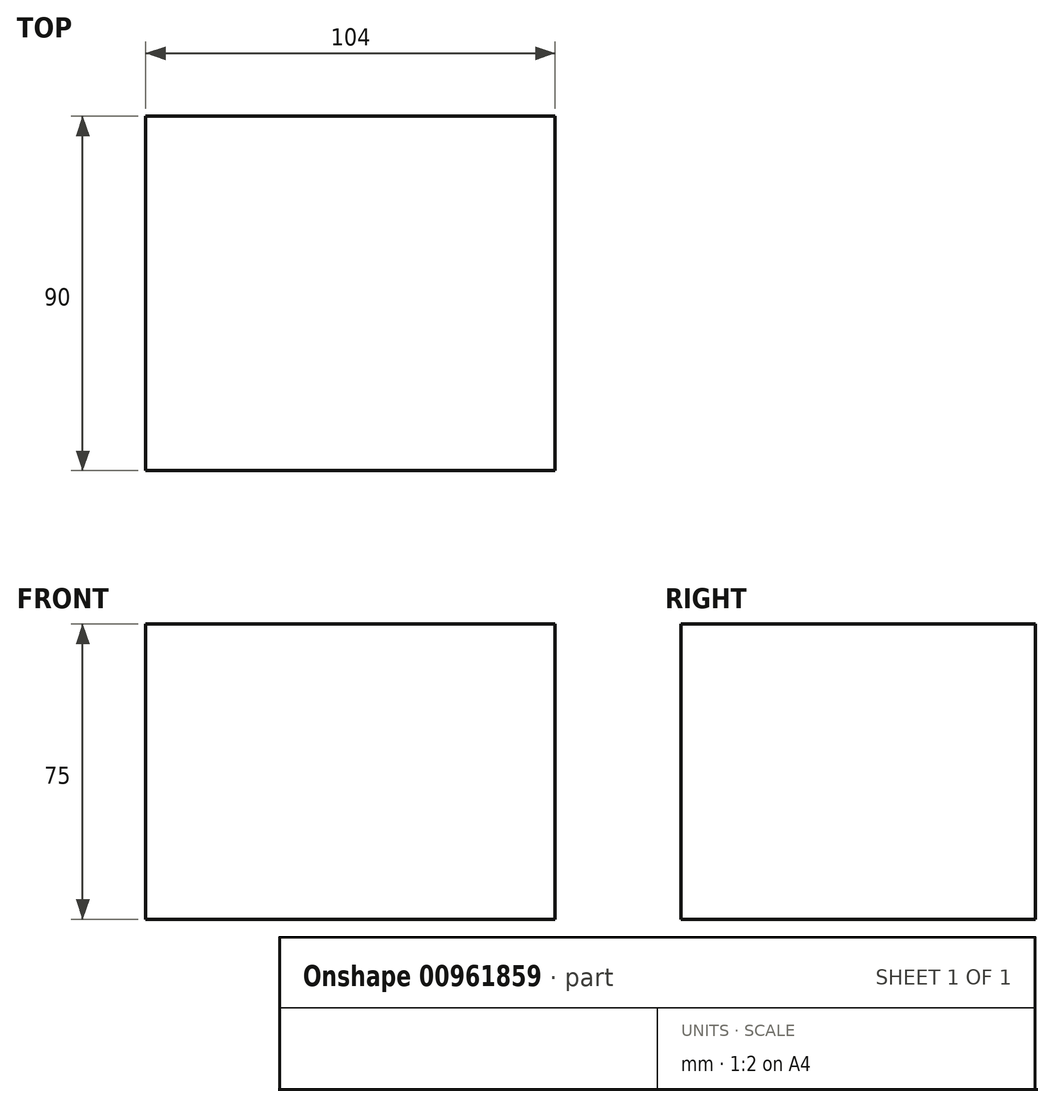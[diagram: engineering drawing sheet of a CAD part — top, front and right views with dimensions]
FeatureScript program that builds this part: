
annotation { "Feature Type Name" : "Feature", "Feature Type Description" : "" }
export const myFeature = defineFeature(function(context is Context, id is Id, definition is map)
    precondition{}
    {
        {
            var Q0;
            Q0=qCreatedBy(makeId("Top.planeOp"),FACE);
            var sketch = newSketch(context, id + "F0", { "sketchPlane" : qUnion([Q0])});
            skLineSegment(sketch, "E0.bottom", {"start": v(-53.37, 53.8) * mm, "end": v(50.63, 53.8) * mm});
            skLineSegment(sketch, "E0.top", {"start": v(-53.37, -36.2) * mm, "end": v(50.63, -36.2) * mm});
            skLineSegment(sketch, "E0.left", {"start": v(-53.37, 53.8) * mm, "end": v(-53.37, -36.2) * mm});
            skLineSegment(sketch, "E0.right", {"start": v(50.63, 53.8) * mm, "end": v(50.63, -36.2) * mm});
            skSolve(sketch);
        }
        {
            var Q0;
            Q0 = qSketchRegion(id + "F0", true);
            extrude(context, id + "F1", {"entities" : qUnion([Q0]), "depth" : 75 * mm, "offsetDistance" : 25 * mm});
        }
    });
